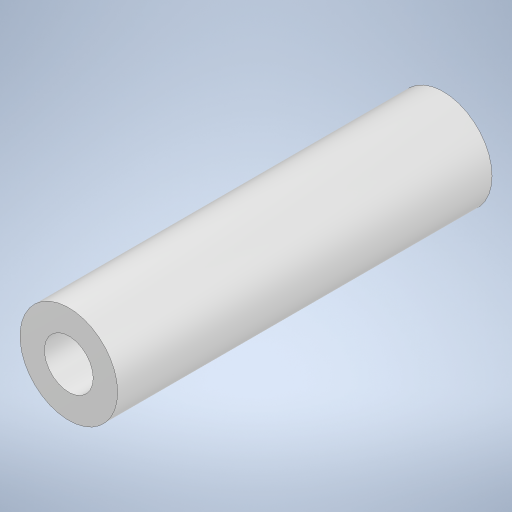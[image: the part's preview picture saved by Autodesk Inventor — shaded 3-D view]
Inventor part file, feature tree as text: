
AUTODESK INVENTOR PART (.ipt)
format: ipt  version: 2023 (Build 270158000, 158)  size: 258,048 bytes
history: native  units: mm
features: extrude x1, sketch x1
ambient origin geometry x8: Origin, YZ Plane, XZ Plane, XY Plane, X Axis, Y Axis, Z Axis, Center Point
bodies: Solid1 (feature_tree)
feature tree (2):
  extrude  "Extrusion1"  Depth=23.0mm
  sketch  "Sketch1"  dims[d0=3.0mm d1=6.0mm d2=23.0mm d3=0.0mm d4=0.5mm d5=0.872665mm d6=0.5mm d7=0.872665mm]
